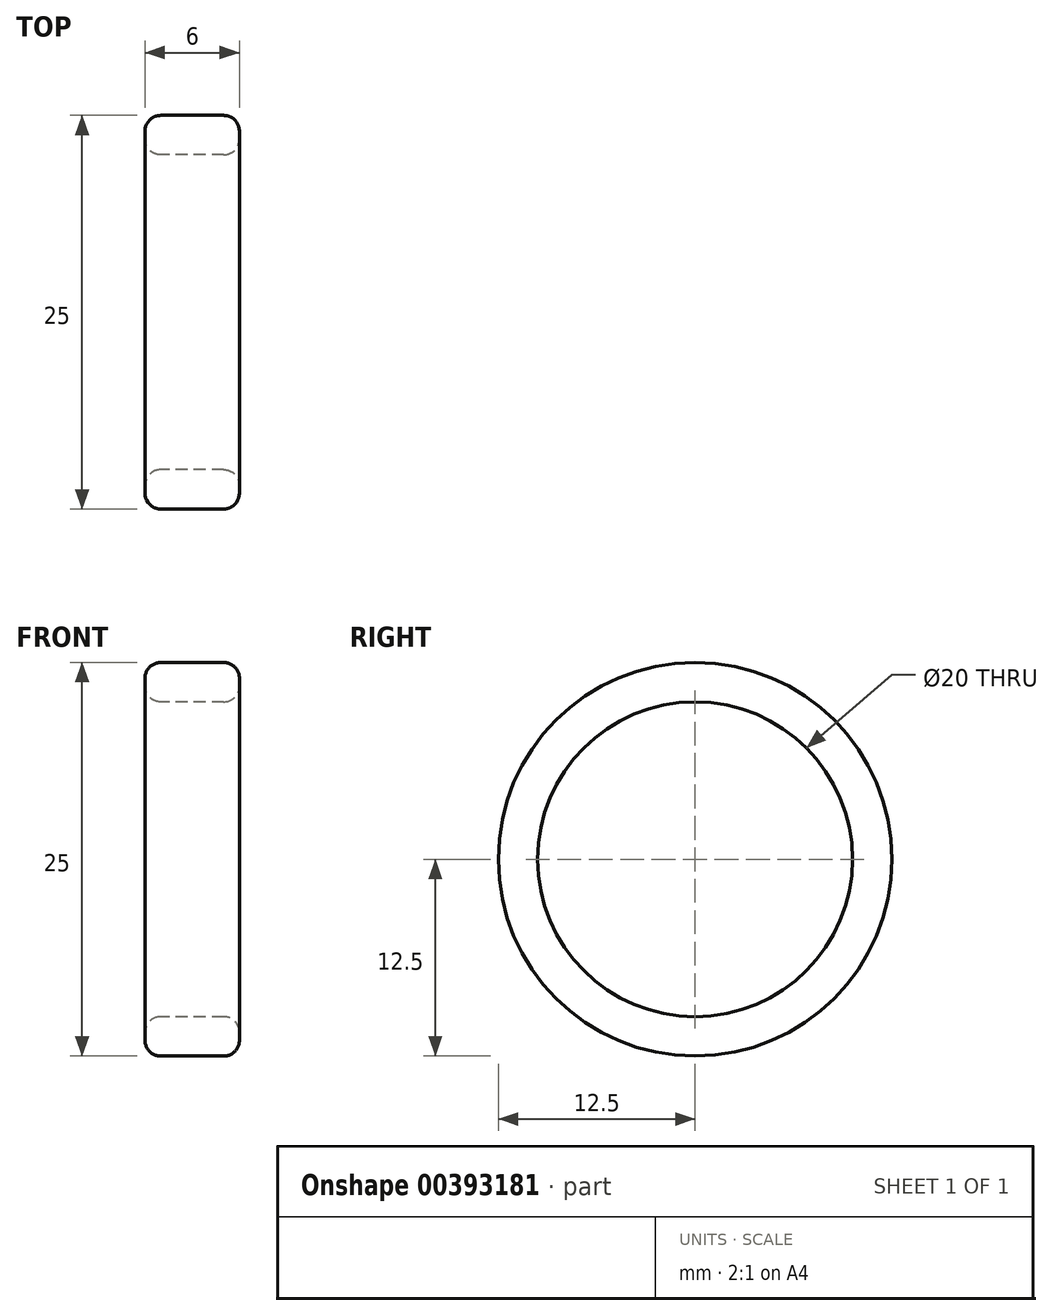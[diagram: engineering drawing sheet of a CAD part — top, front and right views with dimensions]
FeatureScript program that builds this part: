
annotation { "Feature Type Name" : "Feature", "Feature Type Description" : "" }
export const myFeature = defineFeature(function(context is Context, id is Id, definition is map)
    precondition{}
    {
        {
            var Q0;
            Q0=qCreatedBy(makeId("Right.planeOp"),FACE);
            var sketch = newSketch(context, id + "F0", { "sketchPlane" : qUnion([Q0])});
            skCircle(sketch, "E0", {"center": v(0, 0) * mm, "radius": 10 * mm});
            skCircle(sketch, "E1", {"center": v(0, 0) * mm, "radius": 12.5 * mm});
            skSolve(sketch);
        }
        {
            var Q0;
            Q0=makeQuery(id+"F0.imprint","IMPRINT",FACE,{"disambiguationData":[TD([[makeQuery(id+"F0.imprint","IMPRINT",EDGE,{"derivedFrom":sQuery(id+"F0.wireOp",EDGE,"E0")}),-1.0]])]});
            extrude(context, id + "F1", {"entities" : qUnion([Q0]), "endBound" : BoundingType.SYMMETRIC, "depth" : 6 * mm});
        }
        {
            var Q0;
            Q0=makeQuery(id+"F1.opExtrude","CAP_EDGE",EDGE,{"disambiguationData":[OSD([sQuery(id+"F0.wireOp",EDGE,"E1")])],"isStart":false});
            var Q1;
            Q1=makeQuery(id+"F1.opExtrude","CAP_EDGE",EDGE,{"disambiguationData":[OSD([sQuery(id+"F0.wireOp",EDGE,"E0")])],"isStart":false});
            var Q2;
            Q2=makeQuery(id+"F1.opExtrude","CAP_EDGE",EDGE,{"disambiguationData":[OSD([sQuery(id+"F0.wireOp",EDGE,"E0")])],"isStart":true});
            var Q3;
            Q3=makeQuery(id+"F1.opExtrude","CAP_EDGE",EDGE,{"disambiguationData":[OSD([sQuery(id+"F0.wireOp",EDGE,"E1")])],"isStart":true});
            fillet(context, id + "F2", {"entities" : qUnion([Q0, Q1, Q2, Q3]), "radius" : 1 * mm, "tangentPropagation" : true, "allowEdgeOverflow" : false});
        }
    });
